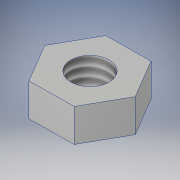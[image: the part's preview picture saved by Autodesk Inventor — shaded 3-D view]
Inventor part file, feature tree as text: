
AUTODESK INVENTOR PART (.ipt)
format: ipt  version: 2018 (Build 220112000, 112)  size: 103,936 bytes
history: native  units: in
note: dims shown in document units (in); Inventor stores cm internally (conversion verified against a paired STEP export)
features: extrude x1, thread x1, sketch x1
ambient origin geometry x8: Origin, YZ Plane, XZ Plane, XY Plane, X Axis, Y Axis, Z Axis, Center Point
bodies: Solid1 (feature_tree)
feature tree (3):
  extrude  "Extrusion1"  Depth=0.1145in
  thread  "Thread1"  [1 undecoded]
  sketch  "Sketch1"  dims[d0=0.27in d1=0.1335in d2=0.1145in d3=0.0in d4=1.0in d5=0.0in]
note: 1 required parameter value undecoded (feature->parameter linkage not recoverable at this tier; creation-order binding heuristic only, values carry confidence <= 0.55)
